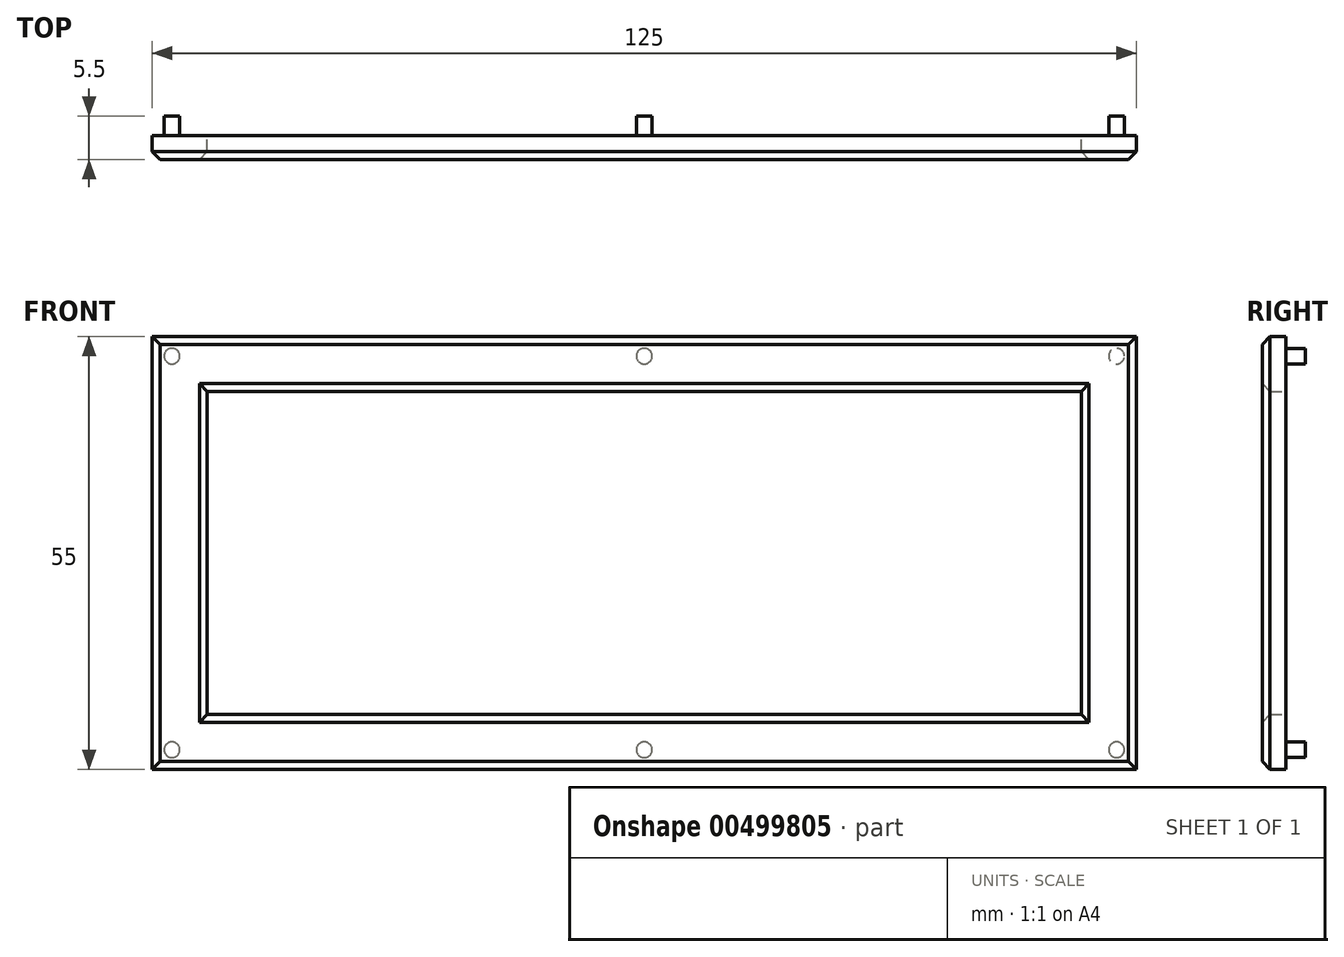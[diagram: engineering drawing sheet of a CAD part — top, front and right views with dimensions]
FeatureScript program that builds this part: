
annotation { "Feature Type Name" : "Feature", "Feature Type Description" : "" }
export const myFeature = defineFeature(function(context is Context, id is Id, definition is map)
    precondition{}
    {
        {
            var Q0;
            Q0=qCreatedBy(makeId("Front.planeOp"),FACE);
            var sketch = newSketch(context, id + "F0", { "sketchPlane" : qUnion([Q0])});
            skLineSegment(sketch, "E0", {"start": v(0, 0) * mm, "end": v(125, 0) * mm});
            skLineSegment(sketch, "E1", {"start": v(125, 0) * mm, "end": v(125, 55) * mm});
            skLineSegment(sketch, "E2", {"start": v(125, 55) * mm, "end": v(0, 55) * mm});
            skLineSegment(sketch, "E3", {"start": v(0, 55) * mm, "end": v(0, 0) * mm});
            skLineSegment(sketch, "E4.0", {"start": v(118, 48) * mm, "end": v(7, 48) * mm});
            skLineSegment(sketch, "E4.1", {"start": v(118, 7) * mm, "end": v(118, 48) * mm});
            skLineSegment(sketch, "E4.2", {"start": v(7, 7) * mm, "end": v(118, 7) * mm});
            skLineSegment(sketch, "E4.3", {"start": v(7, 48) * mm, "end": v(7, 7) * mm});
            skSolve(sketch);
        }
        {
            var Q0;
            Q0=makeQuery(id+"F0.imprint","IMPRINT",FACE,{"disambiguationData":[TD([[makeQuery(id+"F0.imprint","IMPRINT",EDGE,{"derivedFrom":sQuery(id+"F0.wireOp",EDGE,"E0")}),1.0]])]});
            extrude(context, id + "F1", {"entities" : qUnion([Q0]), "depth" : 3 * mm});
        }
        {
            var Q0;
            Q0=makeQuery(id+"F1.opExtrude","CAP_FACE",FACE,{"disambiguationData":[OSD([sQuery(id+"F0.wireOp",EDGE,"E0"),sQuery(id+"F0.wireOp",EDGE,"E1"),sQuery(id+"F0.wireOp",EDGE,"E2"),sQuery(id+"F0.wireOp",EDGE,"E3"),sQuery(id+"F0.wireOp",EDGE,"E4.0"),sQuery(id+"F0.wireOp",EDGE,"E4.1"),sQuery(id+"F0.wireOp",EDGE,"E4.2"),sQuery(id+"F0.wireOp",EDGE,"E4.3")])],"isStart":true});
            var sketch = newSketch(context, id + "F2", { "sketchPlane" : qUnion([Q0])});
            skCircle(sketch, "E5", {"center": v(-122.5, 52.5) * mm, "radius": 1 * mm});
            skCircle(sketch, "E6", {"center": v(-62.5, 52.5) * mm, "radius": 1 * mm});
            skCircle(sketch, "E7", {"center": v(-2.5, 52.5) * mm, "radius": 1 * mm});
            skCircle(sketch, "E8", {"center": v(-2.5, 2.5) * mm, "radius": 1 * mm});
            skCircle(sketch, "E9", {"center": v(-62.5, 2.5) * mm, "radius": 1 * mm});
            skCircle(sketch, "E10", {"center": v(-122.5, 2.5) * mm, "radius": 1 * mm});
            skSolve(sketch);
        }
        {
            var Q0;
            Q0=makeQuery(id+"F2.imprint","IMPRINT",FACE,{"disambiguationData":[TD([[makeQuery(id+"F2.imprint","IMPRINT",EDGE,{"derivedFrom":sQuery(id+"F2.wireOp",EDGE,"E7")}),1.0]])]});
            var Q1;
            Q1=makeQuery(id+"F2.imprint","IMPRINT",FACE,{"disambiguationData":[TD([[makeQuery(id+"F2.imprint","IMPRINT",EDGE,{"derivedFrom":sQuery(id+"F2.wireOp",EDGE,"E9")}),1.0]])]});
            var Q2;
            Q2=makeQuery(id+"F2.imprint","IMPRINT",FACE,{"disambiguationData":[TD([[makeQuery(id+"F2.imprint","IMPRINT",EDGE,{"derivedFrom":sQuery(id+"F2.wireOp",EDGE,"E5")}),1.0]])]});
            var Q3;
            Q3=makeQuery(id+"F2.imprint","IMPRINT",FACE,{"disambiguationData":[TD([[makeQuery(id+"F2.imprint","IMPRINT",EDGE,{"derivedFrom":sQuery(id+"F2.wireOp",EDGE,"E10")}),1.0]])]});
            var Q4;
            Q4=makeQuery(id+"F2.imprint","IMPRINT",FACE,{"disambiguationData":[TD([[makeQuery(id+"F2.imprint","IMPRINT",EDGE,{"derivedFrom":sQuery(id+"F2.wireOp",EDGE,"E6")}),1.0]])]});
            var Q5;
            Q5=makeQuery(id+"F2.imprint","IMPRINT",FACE,{"disambiguationData":[TD([[makeQuery(id+"F2.imprint","IMPRINT",EDGE,{"derivedFrom":sQuery(id+"F2.wireOp",EDGE,"E8")}),1.0]])]});
            var Q6;
            Q6=sQuery(id+"F2.wireOp",EDGE,"E6");
            var Q7;
            Q7=sQuery(id+"F2.wireOp",EDGE,"E7");
            var Q8;
            Q8=sQuery(id+"F2.wireOp",EDGE,"E8");
            var Q9;
            Q9=sQuery(id+"F2.wireOp",EDGE,"E9");
            var Q10;
            Q10=sQuery(id+"F2.wireOp",EDGE,"E10");
            var Q11;
            Q11=sQuery(id+"F2.wireOp",EDGE,"E5");
            extrude(context, id + "F3", {"entities" : qUnion([Q0, Q1, Q2, Q3, Q4, Q5]), "operationType" : NewBodyOperationType.ADD, "surfaceEntities" : qUnion([Q6, Q7, Q8, Q9, Q10, Q11]), "depth" : 2.5 * mm});
        }
        {
            var Q0;
            Q0=makeQuery(id+"F1.opExtrude","CAP_FACE",FACE,{"disambiguationData":[OSD([sQuery(id+"F0.wireOp",EDGE,"E0"),sQuery(id+"F0.wireOp",EDGE,"E1"),sQuery(id+"F0.wireOp",EDGE,"E2"),sQuery(id+"F0.wireOp",EDGE,"E3"),sQuery(id+"F0.wireOp",EDGE,"E4.0"),sQuery(id+"F0.wireOp",EDGE,"E4.1"),sQuery(id+"F0.wireOp",EDGE,"E4.2"),sQuery(id+"F0.wireOp",EDGE,"E4.3")])],"isStart":false});
            chamfer(context, id + "F4", {"entities" : qUnion([Q0]), "width" : 1 * mm, "tangentPropagation" : true});
        }
    });
